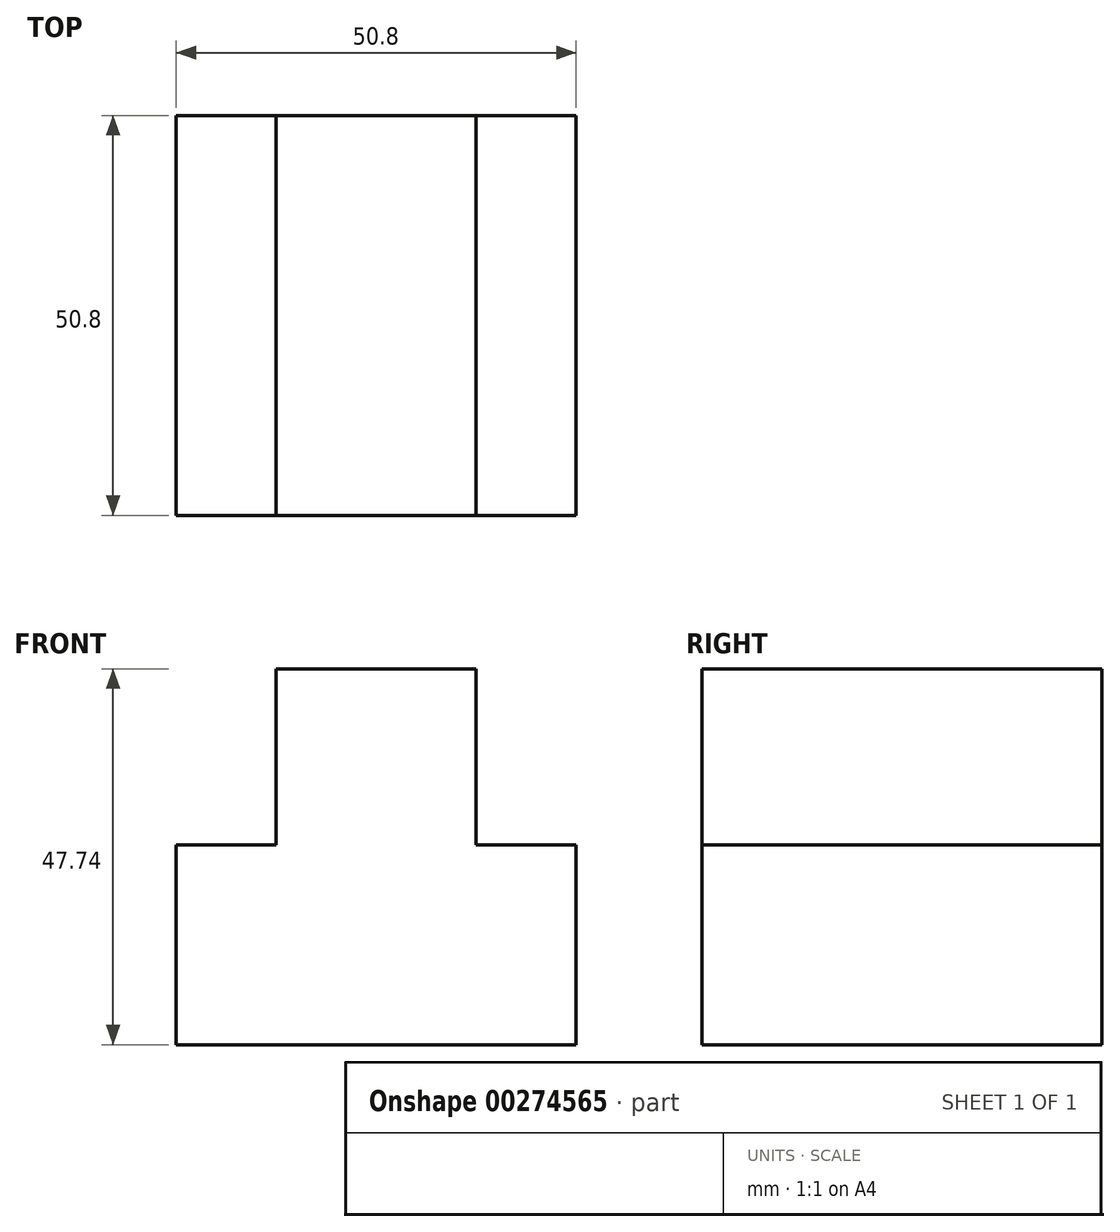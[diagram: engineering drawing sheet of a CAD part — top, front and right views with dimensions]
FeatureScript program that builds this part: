
annotation { "Feature Type Name" : "Feature", "Feature Type Description" : "" }
export const myFeature = defineFeature(function(context is Context, id is Id, definition is map)
    precondition{}
    {
        {
            var Q0;
            Q0=qCreatedBy(makeId("Front.planeOp"),FACE);
            var sketch = newSketch(context, id + "F0", { "sketchPlane" : qUnion([Q0])});
            skLineSegment(sketch, "E0", {"start": v(0, 0) * mm, "end": v(-50.8, 0) * mm});
            skLineSegment(sketch, "E1", {"start": v(-50.8, 0) * mm, "end": v(-50.8, 25.4) * mm});
            skLineSegment(sketch, "E2", {"start": v(-50.8, 25.4) * mm, "end": v(-38.1, 25.4) * mm});
            skLineSegment(sketch, "E3", {"start": v(-38.1, 25.4) * mm, "end": v(-38.1, 38.1) * mm});
            skLineSegment(sketch, "E4", {"start": v(-38.1, 38.1) * mm, "end": v(-38.1, 47.74) * mm});
            skLineSegment(sketch, "E5", {"start": v(-38.1, 47.74) * mm, "end": v(-12.7, 47.74) * mm});
            skLineSegment(sketch, "E6", {"start": v(-12.7, 47.74) * mm, "end": v(-12.7, 25.4) * mm});
            skLineSegment(sketch, "E7", {"start": v(-12.7, 25.4) * mm, "end": v(0, 25.4) * mm});
            skLineSegment(sketch, "E8", {"start": v(0, 25.4) * mm, "end": v(0, 0) * mm});
            skSolve(sketch);
        }
        {
            var Q0;
            Q0 = qSketchRegion(id + "F0", true);
            extrude(context, id + "F1", {"entities" : qUnion([Q0]), "depth" : 50.8 * mm});
        }
    });
